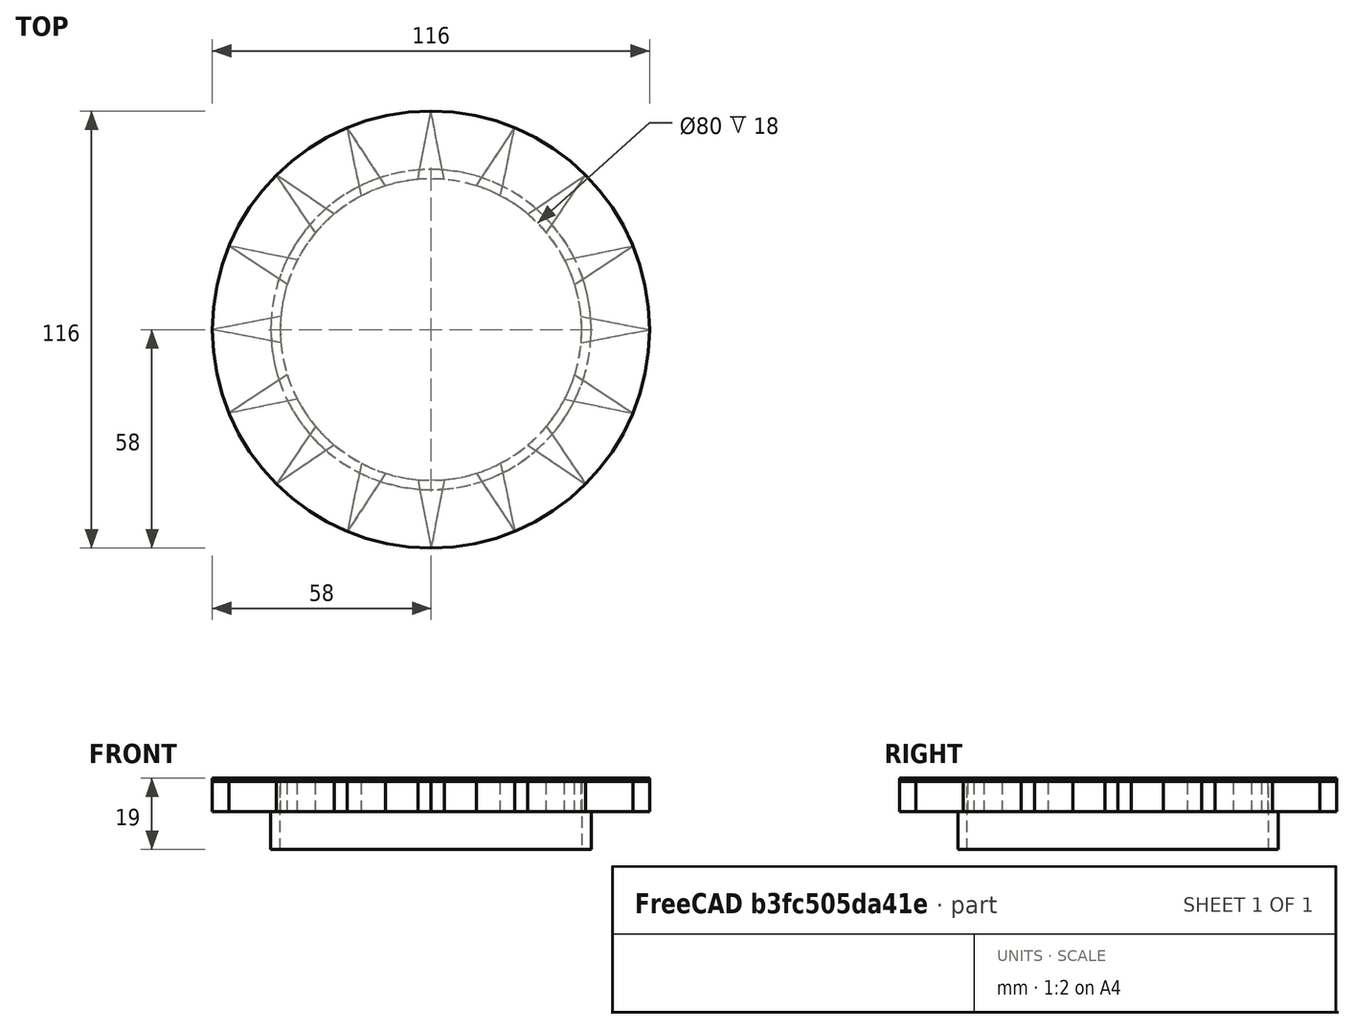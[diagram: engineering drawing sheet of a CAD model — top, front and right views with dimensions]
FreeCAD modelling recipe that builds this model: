
FCSTD DOCUMENT  (FreeCAD 0.21R33694 (Git))
Label: kitchen
License: Creative Commons Attribution 4.0
LicenseURL: https://creativecommons.org/licenses/by/4.0/
objects: PartDesign::AdditiveCylinder×2, PartDesign::AdditiveWedge×1, PartDesign::PolarPattern×1, PartDesign::SubtractiveCylinder×1, PartDesign::Body×1, Mesh::Feature×1
note: 10 computed .brp shape members not serialized (recipe doc carries the construction recipe); baked Part::Feature solids carry a one-line shape summary decoded from their .brp

FEATURE [PartDesign::AdditiveCylinder] Cylinder004
  Angle = 360
  AttacherType = Attacher::AttachEngine3D
  FirstAngle = 0
  Height = 1
  MapMode = 5
  Radius = 58
  SecondAngle = 0
  Support = -> [XY_Plane]
  expr: Radius = 116 / 2
FEATURE [PartDesign::AdditiveWedge] Wedge
  AttacherType = Attacher::AttachEngine3D
  AttachmentOffset = pos=(-5,48,0) rot=(0,0,1;0rad)
  BaseFeature = -> Cylinder004
  Placement = pos=(-5,-48,-5.9e-15) rot=(1,0,0;3.14159rad)
  Support = -> [Cylinder004,Origin]
  X2max = 5
  X2min = 5
  Xmax = 10
  Xmin = 0
  Ymax = 10
  Ymin = -16
  Z2max = 8
  Z2min = 0
  Zmax = 8
  Zmin = 0
FEATURE [PartDesign::PolarPattern] PolarPattern
  Angle = 360
  Axis = -> Z_Axis
  BaseFeature = -> Wedge
  Occurrences = 16
  Originals = -> [Wedge]
  Placement = pos=(-5,-48,-5.9e-15) rot=(1,0,0;3.14159rad)
FEATURE [PartDesign::AdditiveCylinder] Cylinder
  Angle = 360
  AttacherType = Attacher::AttachEngine3D
  AttachmentOffset = pos=(0,0,8) rot=(0,0,1;0rad)
  BaseFeature = -> PolarPattern
  FirstAngle = 0
  Height = 10
  MapMode = 5
  Placement = pos=(0,0,-8) rot=(1,0,0;3.14159rad)
  Radius = 42.5
  SecondAngle = 0
  Support = -> [Cylinder004]
FEATURE [PartDesign::SubtractiveCylinder] Cylinder005
  Angle = 360
  AttacherType = Attacher::AttachEngine3D
  AttachmentOffset = pos=(0,0,-18) rot=(0,0,1;0rad)
  BaseFeature = -> Cylinder
  FirstAngle = 0
  Height = 18
  MapMode = 5
  Placement = pos=(0,0,0) rot=(1,0,0;3.14159rad)
  Radius = 40
  SecondAngle = 0
  Support = -> [Cylinder]
FEATURE [PartDesign::Body] Body
  Group = -> [Cylinder004,Wedge,PolarPattern,Cylinder,Cylinder005]
  Origin = -> Origin
  Tip = -> Cylinder005
FEATURE [Mesh::Feature] Mesh  label="Body (Meshed)"
